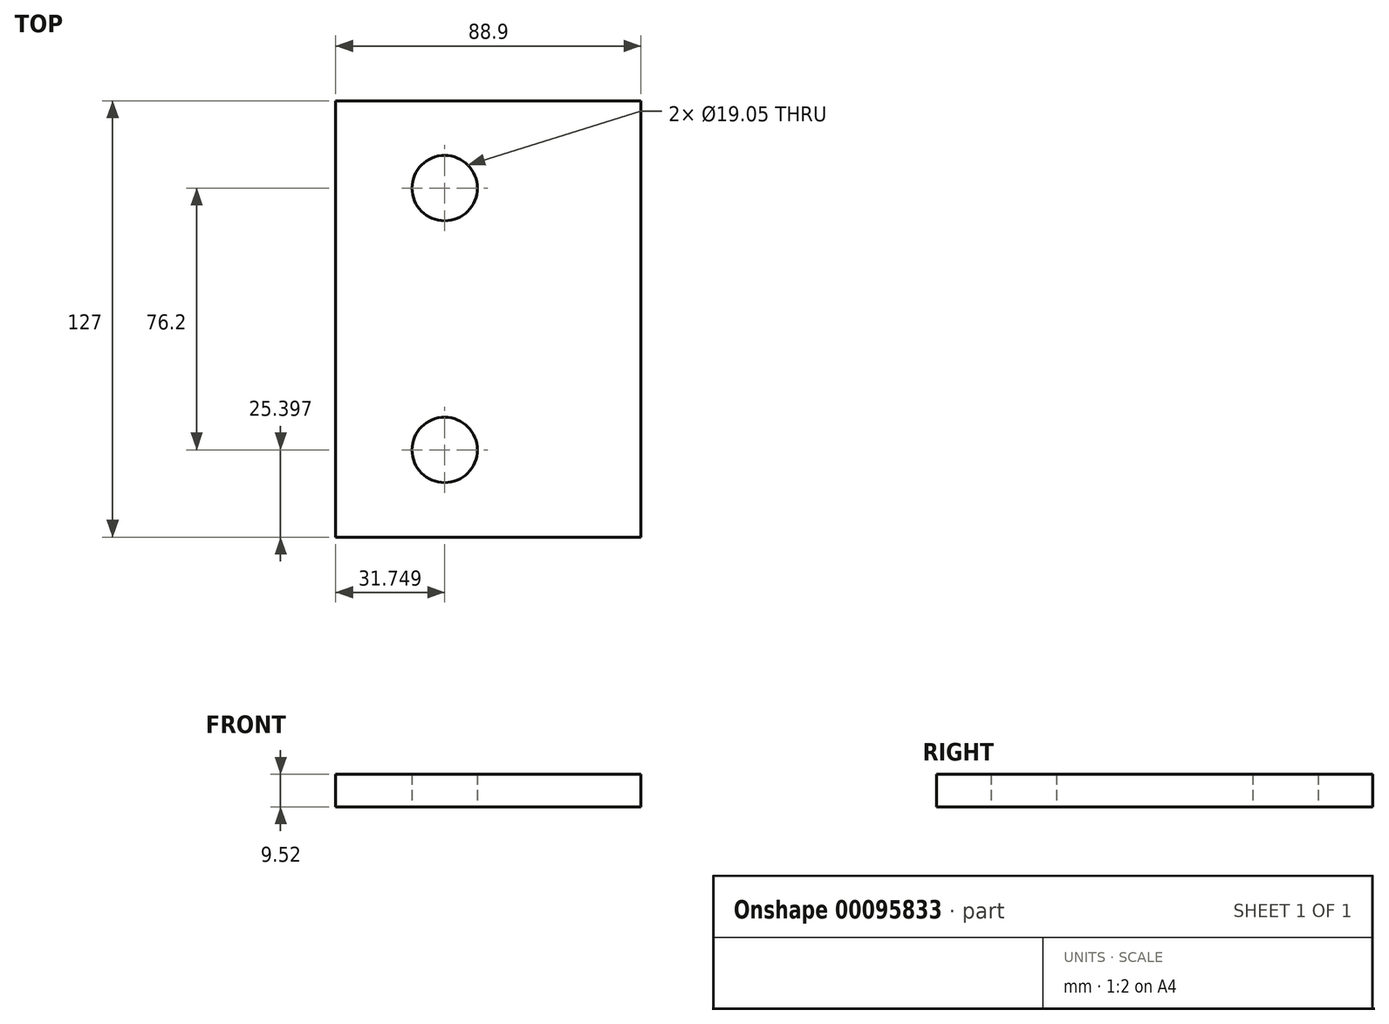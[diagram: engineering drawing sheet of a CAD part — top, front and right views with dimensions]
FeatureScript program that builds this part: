
annotation { "Feature Type Name" : "Feature", "Feature Type Description" : "" }
export const myFeature = defineFeature(function(context is Context, id is Id, definition is map)
    precondition{}
    {
        {
            var Q0;
            Q0=qCreatedBy(makeId("Top.planeOp"),FACE);
            var sketch = newSketch(context, id + "F0", { "sketchPlane" : qUnion([Q0]), "disableImprinting" : false});
            skLineSegment(sketch, "E0.bottom", {"start": v(-63.18, 61.32) * mm, "end": v(25.72, 61.32) * mm});
            skLineSegment(sketch, "E0.top", {"start": v(-63.18, -65.68) * mm, "end": v(25.72, -65.68) * mm});
            skLineSegment(sketch, "E0.left", {"start": v(-63.18, 61.32) * mm, "end": v(-63.18, -65.68) * mm});
            skLineSegment(sketch, "E0.right", {"start": v(25.72, 61.32) * mm, "end": v(25.72, -65.68) * mm});
            skLineSegment(sketch, "E1", {"start": v(-63.18, -2.18) * mm, "end": v(25.72, -2.18) * mm, "construction": true});
            skCircle(sketch, "E2", {"center": v(-31.43, 35.92) * mm, "radius": 9.53 * mm});
            skCircle(sketch, "E3", {"center": v(-31.43, -40.28) * mm, "radius": 9.53 * mm});
            skLineSegment(sketch, "E4", {"start": v(-31.43, 35.92) * mm, "end": v(-31.43, -40.28) * mm, "construction": true});
            skSolve(sketch);
        }
        {
            var Q0;
            Q0=makeQuery(id+"F0.imprint","IMPRINT",FACE,{"disambiguationData":[TD([[makeQuery(id+"F0.imprint","IMPRINT",EDGE,{"derivedFrom":sQuery(id+"F0.wireOp",EDGE,"E0.bottom")}),-1.0]])]});
            extrude(context, id + "F1", {"entities" : qUnion([Q0]), "depth" : 9.52 * mm, "symmetric" : true});
        }
    });
